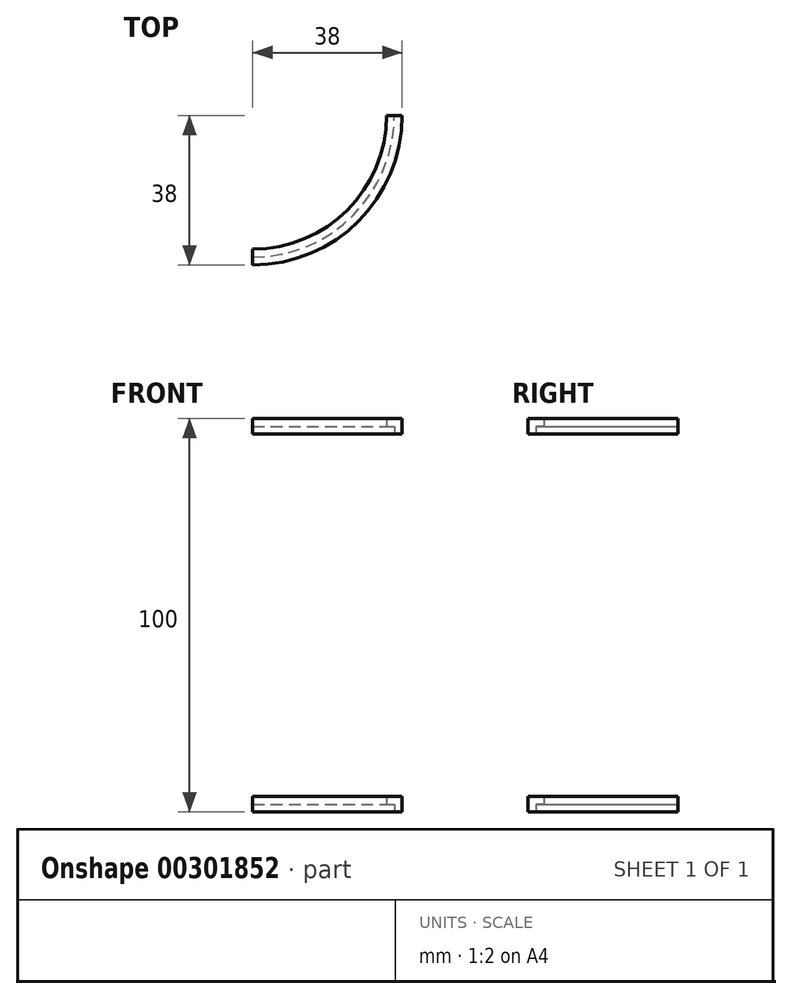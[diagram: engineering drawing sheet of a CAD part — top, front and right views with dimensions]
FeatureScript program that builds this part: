
annotation { "Feature Type Name" : "Feature", "Feature Type Description" : "" }
export const myFeature = defineFeature(function(context is Context, id is Id, definition is map)
    precondition{}
    {
        {
            var Q0;
            Q0=qCreatedBy(makeId("Front.planeOp"),FACE);
            var sketch = newSketch(context, id + "F0", { "sketchPlane" : qUnion([Q0])});
            skLineSegment(sketch, "E0", {"start": v(-41.52, 48.93) * mm, "end": v(-41.52, -51.07) * mm});
            skLineSegment(sketch, "E1.bottom", {"start": v(-7.52, 48.93) * mm, "end": v(-6.02, 48.93) * mm});
            skLineSegment(sketch, "E1.top", {"start": v(-7.52, -51.07) * mm, "end": v(-6.02, -51.07) * mm});
            skLineSegment(sketch, "E1.left", {"start": v(-7.52, 48.93) * mm, "end": v(-7.52, -51.07) * mm});
            skLineSegment(sketch, "E1.right", {"start": v(-6.02, 48.93) * mm, "end": v(-6.02, -51.07) * mm});
            skSolve(sketch);
        }
        {
            var Q0;
            Q0=sQuery(id+"F0.wireOp",EDGE,"E1.left");
            var Q1;
            Q1=sQuery(id+"F0.wireOp",EDGE,"E0");
            revolve(context, id + "F1", {"bodyType" : ToolBodyType.SURFACE, "surfaceEntities" : qUnion([Q0]), "axis" : qUnion([Q1]), "revolveType" : RevolveType.ONE_DIRECTION, "angle" : 80 * degree});
        }
        {
            var Q0;
            Q0=qCreatedBy(makeId("Front.planeOp"),FACE);
            var sketch = newSketch(context, id + "F2", { "sketchPlane" : qUnion([Q0])});
            skLineSegment(sketch, "E2.bottom", {"start": v(36.83, 49) * mm, "end": v(40.83, 49) * mm});
            skLineSegment(sketch, "E2.left", {"start": v(36.83, 49) * mm, "end": v(36.83, 47) * mm});
            skLineSegment(sketch, "E2.right", {"start": v(40.83, 49) * mm, "end": v(40.83, 47) * mm});
            skLineSegment(sketch, "E3.top", {"start": v(40.83, 45) * mm, "end": v(38.83, 45) * mm});
            skLineSegment(sketch, "E3.left", {"start": v(40.83, 47) * mm, "end": v(40.83, 45) * mm});
            skLineSegment(sketch, "E3.right", {"start": v(38.83, 47) * mm, "end": v(38.83, 45) * mm});
            skLineSegment(sketch, "E4", {"start": v(36.83, 47) * mm, "end": v(38.83, 47) * mm});
            skLineSegment(sketch, "E5", {"start": v(2.83, 49) * mm, "end": v(2.83, 44.27) * mm});
            skSolve(sketch);
        }
        {
            var Q0;
            Q0=makeQuery(id+"F2.imprint","IMPRINT",FACE,{"disambiguationData":[TD([[makeQuery(id+"F2.imprint","IMPRINT",EDGE,{"derivedFrom":sQuery(id+"F2.wireOp",EDGE,"E2.bottom")}),-1.0]])]});
            var Q1;
            Q1=sQuery(id+"F2.wireOp",EDGE,"E5");
            revolve(context, id + "F3", {"entities" : qUnion([Q0]), "axis" : qUnion([Q1]), "revolveType" : RevolveType.ONE_DIRECTION, "angle" : 90 * degree});
        }
        {
            var Q0;
            Q0=makeQuery(id+"F3.opRevolve","SWEPT_BODY",BODY,{"disambiguationData":[OSD([sQuery(id+"F2.wireOp",EDGE,"E2.bottom"),sQuery(id+"F2.wireOp",EDGE,"E2.left"),sQuery(id+"F2.wireOp",EDGE,"E2.right"),sQuery(id+"F2.wireOp",EDGE,"E3.top"),sQuery(id+"F2.wireOp",EDGE,"E3.left"),sQuery(id+"F2.wireOp",EDGE,"E3.right"),sQuery(id+"F2.wireOp",EDGE,"E4")])]});
            transform(context, id + "F4", {"entities" : qUnion([Q0]), "transformType" : TransformType.COPY});
        }
        {
            var Q0;
            Q0=makeQuery(id+"FAOt3OC8HXCrhzc_2.opRevolve","SWEPT_BODY",BODY,{"disambiguationData":[OSD([sQuery(id+"FHKGgw05aPyslrg_2.wireOp",EDGE,"12e0f708-c617-4aad-ab6b-b1c40541b02d.bottom"),sQuery(id+"FHKGgw05aPyslrg_2.wireOp",EDGE,"12e0f708-c617-4aad-ab6b-b1c40541b02d.left"),sQuery(id+"FHKGgw05aPyslrg_2.wireOp",EDGE,"12e0f708-c617-4aad-ab6b-b1c40541b02d.right"),sQuery(id+"FHKGgw05aPyslrg_2.wireOp",EDGE,"e9ed1381-d629-44c2-a1b2-1e7b23078c9e.top"),sQuery(id+"FHKGgw05aPyslrg_2.wireOp",EDGE,"e9ed1381-d629-44c2-a1b2-1e7b23078c9e.left"),sQuery(id+"FHKGgw05aPyslrg_2.wireOp",EDGE,"e9ed1381-d629-44c2-a1b2-1e7b23078c9e.right"),sQuery(id+"FHKGgw05aPyslrg_2.wireOp",EDGE,"b97620f2-9fae-429f-9132-152a9f78053c")])]});
            var Q1;
            Q1=makeQuery(id+"F3.opRevolve","SWEPT_BODY",BODY,{"disambiguationData":[OSD([sQuery(id+"F2.wireOp",EDGE,"E2.bottom"),sQuery(id+"F2.wireOp",EDGE,"E2.left"),sQuery(id+"F2.wireOp",EDGE,"E2.right"),sQuery(id+"F2.wireOp",EDGE,"E3.top"),sQuery(id+"F2.wireOp",EDGE,"E3.left"),sQuery(id+"F2.wireOp",EDGE,"E3.right"),sQuery(id+"F2.wireOp",EDGE,"E4")])]});
            var Q2;
            Q2=qCreatedBy(makeId("Top.planeOp"),FACE);
            transform(context, id + "F5", {"entities" : qUnion([Q0, Q1]), "transformType" : TransformType.TRANSLATION_DISTANCE, "transformDirection" : qUnion([Q2]), "distance" : 100 * mm, "oppositeDirection" : true, "makeCopy" : false});
        }
        {
            var Q0;
            Q0=makeQuery(id+"F3.opRevolve","SWEPT_BODY",BODY,{"disambiguationData":[OSD([sQuery(id+"F2.wireOp",EDGE,"E2.bottom"),sQuery(id+"F2.wireOp",EDGE,"E2.left"),sQuery(id+"F2.wireOp",EDGE,"E2.right"),sQuery(id+"F2.wireOp",EDGE,"E3.top"),sQuery(id+"F2.wireOp",EDGE,"E3.left"),sQuery(id+"F2.wireOp",EDGE,"E3.right"),sQuery(id+"F2.wireOp",EDGE,"E4")])]});
            transform(context, id + "F6", {"entities" : qUnion([Q0]), "transformType" : TransformType.TRANSLATION_3D, "dx" : 0 * mm, "dy" : 30 * mm, "dz" : 4 * mm, "makeCopy" : false});
        }
        {
            var Q0;
            Q0=makeQuery(id+"F3.opRevolve","SWEPT_BODY",BODY,{"disambiguationData":[OSD([sQuery(id+"F2.wireOp",EDGE,"E2.bottom"),sQuery(id+"F2.wireOp",EDGE,"E2.left"),sQuery(id+"F2.wireOp",EDGE,"E2.right"),sQuery(id+"F2.wireOp",EDGE,"E3.top"),sQuery(id+"F2.wireOp",EDGE,"E3.left"),sQuery(id+"F2.wireOp",EDGE,"E3.right"),sQuery(id+"F2.wireOp",EDGE,"E4")])]});
            transform(context, id + "F7", {"entities" : qUnion([Q0]), "transformType" : TransformType.TRANSLATION_3D, "dx" : 0 * mm, "dy" : -30 * mm, "dz" : 0 * mm, "makeCopy" : false});
        }
    });
